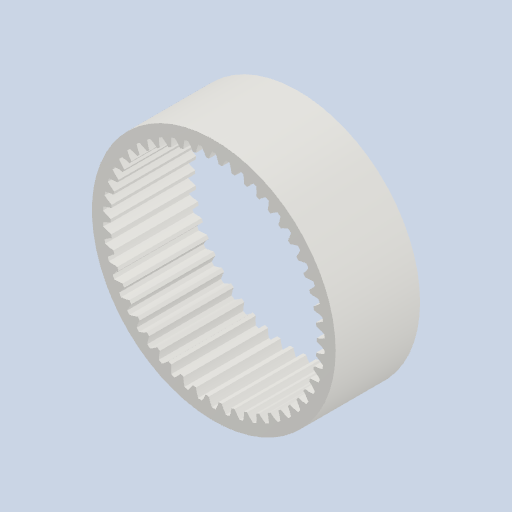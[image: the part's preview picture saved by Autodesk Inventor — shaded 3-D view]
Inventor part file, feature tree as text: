
AUTODESK INVENTOR PART (.ipt)
format: ipt  version: 2022 (Build 260153000, 153)  size: 364,544 bytes
history: native  units: mm (DEFAULTED — no unit token found)
features: plane x3, other x3, sketch x2, extrude x1
ambient origin geometry x8: Origin, YZ Plane, XZ Plane, XY Plane, X Axis, Y Axis, Z Axis, Center Point
bodies: Solid1 (feature_tree)
feature tree (9):
  extrude  "Extrusion1"  Depth=20.0mm TaperAngle=0.0deg
  plane  "Work Plane2"
  plane  "Work Plane8"
  plane  "Work Plane9"
  other  "Цилиндрическое зубчатое зацепление"
  sketch  "Sketch1"  dims[d0=57.75mm d1=20.0mm d2=0.0mm]
  sketch  "Sketch2"  dims[d3=50.0mm d4=10.0mm d5=0.0mm d16=19.5mm d17=0.0mm d34=0.628319mm d39=0.0mm d45=0.0mm d47=19.5mm d50=0.0mm d51=0.0mm d52=19.5mm]
  other  "Srf1"
  other  "Средний диаметр"
